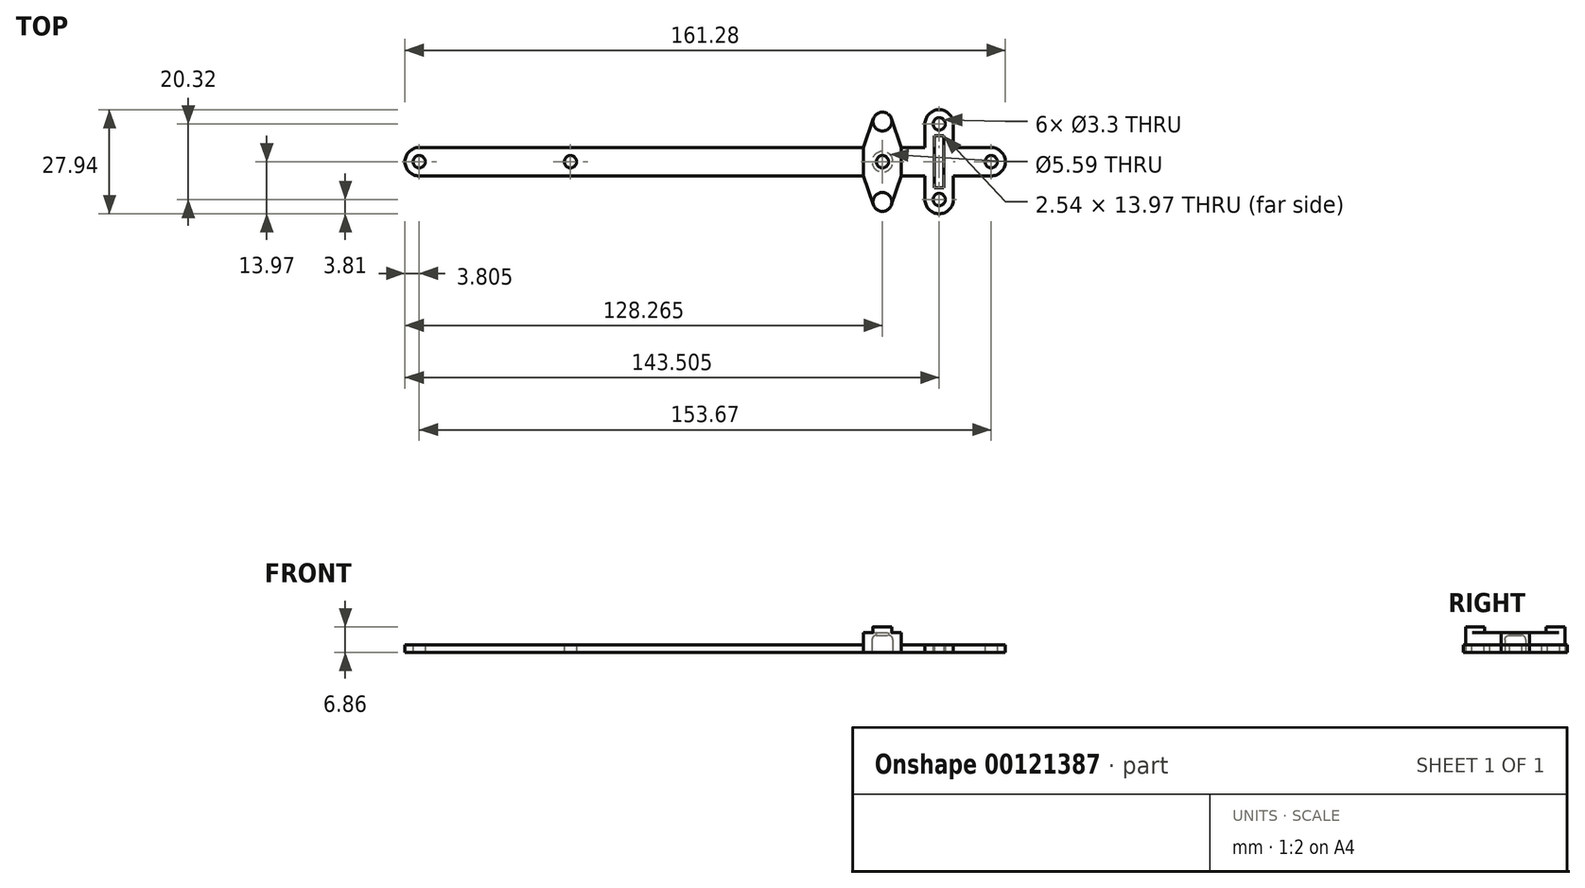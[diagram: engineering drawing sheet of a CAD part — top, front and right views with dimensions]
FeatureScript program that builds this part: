
annotation { "Feature Type Name" : "Feature", "Feature Type Description" : "" }
export const myFeature = defineFeature(function(context is Context, id is Id, definition is map)
    precondition{}
    {
        {
            var Q0;
            Q0=qCreatedBy(makeId("Top.planeOp"),FACE);
            var sketch = newSketch(context, id + "F0", { "sketchPlane" : qUnion([Q0])});
            skCircle(sketch, "E0", {"center": v(-76.83, 0) * mm, "radius": 1.65 * mm});
            skCircle(sketch, "E1", {"center": v(76.83, 0) * mm, "radius": 1.65 * mm});
            skLineSegment(sketch, "E2", {"start": v(-76.83, 0) * mm, "end": v(76.83, 0) * mm, "construction": true});
            skPoint(sketch, "E3", {"position": v(0, 0) * mm});
            skCircle(sketch, "E4", {"center": v(-36.2, 0) * mm, "radius": 1.65 * mm});
            skCircle(sketch, "E5", {"center": v(62.87, 10.16) * mm, "radius": 1.65 * mm});
            skCircle(sketch, "E6", {"center": v(62.87, -10.16) * mm, "radius": 1.65 * mm});
            skLineSegment(sketch, "E7", {"start": v(62.87, 10.16) * mm, "end": v(62.87, -10.16) * mm, "construction": true});
            skPoint(sketch, "E8", {"position": v(62.87, 0) * mm});
            skCircle(sketch, "E9", {"center": v(47.63, 0) * mm, "radius": 1.65 * mm});
            skLineSegment(sketch, "E10", {"start": v(-76.83, 3.8) * mm, "end": v(42.55, 3.8) * mm});
            skLineSegment(sketch, "E11", {"start": v(59.06, 3.81) * mm, "end": v(59.06, 10.16) * mm});
            skLineSegment(sketch, "E12", {"start": v(66.68, 10.16) * mm, "end": v(66.68, 3.8) * mm});
            skLineSegment(sketch, "E13", {"start": v(66.68, 3.8) * mm, "end": v(76.83, 3.81) * mm});
            skLineSegment(sketch, "E14", {"start": v(-76.83, -3.81) * mm, "end": v(42.55, -3.81) * mm});
            skLineSegment(sketch, "E15", {"start": v(59.06, -3.81) * mm, "end": v(59.06, -10.16) * mm});
            skLineSegment(sketch, "E16", {"start": v(66.68, -10.16) * mm, "end": v(66.68, -3.8) * mm});
            skLineSegment(sketch, "E17", {"start": v(66.68, -3.81) * mm, "end": v(76.84, -3.81) * mm});
            skArc(sketch, "E18", {"start": v(-76.83, 3.8) * mm, "mid": v(-80.64, 0) * mm, "end": v(-76.83, -3.8) * mm});
            skArc(sketch, "E19", {"start": v(66.68, 10.16) * mm, "mid": v(62.87, 13.97) * mm, "end": v(59.06, 10.16) * mm});
            skArc(sketch, "E20", {"start": v(59.06, -10.16) * mm, "mid": v(62.87, -13.97) * mm, "end": v(66.68, -10.16) * mm});
            skArc(sketch, "E21", {"start": v(76.83, -3.8) * mm, "mid": v(80.64, 0) * mm, "end": v(76.83, 3.8) * mm});
            skLineSegment(sketch, "E22", {"start": v(47.63, -10.8) * mm, "end": v(47.63, 10.8) * mm, "construction": true});
            skLineSegment(sketch, "E23", {"start": v(42.55, 3.8) * mm, "end": v(45.22, 11.62) * mm});
            skLineSegment(sketch, "E24", {"start": v(50.03, 11.62) * mm, "end": v(52.7, 3.8) * mm});
            skLineSegment(sketch, "E25", {"start": v(52.7, -3.81) * mm, "end": v(50.03, -11.62) * mm});
            skLineSegment(sketch, "E26", {"start": v(42.55, -3.81) * mm, "end": v(45.22, -11.62) * mm});
            skArc(sketch, "E27", {"start": v(45.22, 11.62) * mm, "mid": v(47.63, 8.25) * mm, "end": v(50.03, 11.62) * mm, "construction": true});
            skArc(sketch, "E28", {"start": v(50.03, 11.62) * mm, "mid": v(47.63, 13.33) * mm, "end": v(45.22, 11.62) * mm});
            skArc(sketch, "E29", {"start": v(45.22, -11.62) * mm, "mid": v(47.63, -13.34) * mm, "end": v(50.03, -11.62) * mm});
            skArc(sketch, "E30", {"start": v(50.03, -11.62) * mm, "mid": v(47.63, -8.26) * mm, "end": v(45.22, -11.62) * mm, "construction": true});
            skLineSegment(sketch, "E31", {"start": v(42.55, 3.8) * mm, "end": v(52.7, 3.8) * mm, "construction": true});
            skLineSegment(sketch, "E32", {"start": v(42.55, -3.81) * mm, "end": v(52.7, -3.81) * mm, "construction": true});
            skLineSegment(sketch, "E33", {"start": v(52.7, -3.81) * mm, "end": v(59.06, -3.81) * mm});
            skLineSegment(sketch, "E34", {"start": v(52.7, 3.8) * mm, "end": v(59.06, 3.8) * mm});
            skLineSegment(sketch, "E35.bottom", {"start": v(61.6, 6.99) * mm, "end": v(64.14, 6.99) * mm});
            skLineSegment(sketch, "E35.top", {"start": v(61.6, -6.99) * mm, "end": v(64.14, -6.99) * mm});
            skLineSegment(sketch, "E35.left", {"start": v(61.6, 6.99) * mm, "end": v(61.6, -6.99) * mm});
            skLineSegment(sketch, "E35.right", {"start": v(64.14, 6.99) * mm, "end": v(64.14, -6.99) * mm});
            skPoint(sketch, "E36", {"position": v(62.87, 6.99) * mm});
            skPoint(sketch, "E37", {"position": v(61.6, 0) * mm});
            skSolve(sketch);
        }
        {
            var Q0;
            Q0 = qSketchRegion(id + "F0", true);
            extrude(context, id + "F1", {"entities" : qUnion([Q0]), "depth" : 2.03 * mm});
        }
        {
            var Q0;
            Q0=makeQuery(id+"F1.opExtrude","CAP_FACE",FACE,{"disambiguationData":[OSD([sQuery(id+"F0.wireOp",EDGE,"E0"),sQuery(id+"F0.wireOp",EDGE,"E1"),sQuery(id+"F0.wireOp",EDGE,"E4"),sQuery(id+"F0.wireOp",EDGE,"E5"),sQuery(id+"F0.wireOp",EDGE,"E6"),sQuery(id+"F0.wireOp",EDGE,"E9"),sQuery(id+"F0.wireOp",EDGE,"E10"),sQuery(id+"F0.wireOp",EDGE,"E11"),sQuery(id+"F0.wireOp",EDGE,"E12"),sQuery(id+"F0.wireOp",EDGE,"E13"),sQuery(id+"F0.wireOp",EDGE,"E14"),sQuery(id+"F0.wireOp",EDGE,"E15"),sQuery(id+"F0.wireOp",EDGE,"E16"),sQuery(id+"F0.wireOp",EDGE,"E17"),sQuery(id+"F0.wireOp",EDGE,"E18"),sQuery(id+"F0.wireOp",EDGE,"E19"),sQuery(id+"F0.wireOp",EDGE,"E20"),sQuery(id+"F0.wireOp",EDGE,"E21"),sQuery(id+"F0.wireOp",EDGE,"E23"),sQuery(id+"F0.wireOp",EDGE,"E24"),sQuery(id+"F0.wireOp",EDGE,"E25"),sQuery(id+"F0.wireOp",EDGE,"E26"),sQuery(id+"F0.wireOp",EDGE,"E28"),sQuery(id+"F0.wireOp",EDGE,"E29"),sQuery(id+"F0.wireOp",EDGE,"E33"),sQuery(id+"F0.wireOp",EDGE,"E34")])],"isStart":false});
            var sketch = newSketch(context, id + "F2", { "sketchPlane" : qUnion([Q0])});
            skLineSegment(sketch, "E38", {"start": v(45.22, 11.62) * mm, "end": v(42.55, 3.8) * mm});
            skLineSegment(sketch, "E39", {"start": v(42.55, 3.8) * mm, "end": v(42.55, -3.81) * mm});
            skLineSegment(sketch, "E40", {"start": v(42.55, -3.81) * mm, "end": v(45.22, -11.62) * mm});
            skLineSegment(sketch, "E41", {"start": v(50.03, 11.62) * mm, "end": v(52.7, 3.8) * mm});
            skLineSegment(sketch, "E42", {"start": v(52.7, 3.8) * mm, "end": v(52.7, -3.81) * mm});
            skLineSegment(sketch, "E43", {"start": v(52.7, -3.81) * mm, "end": v(50.03, -11.62) * mm});
            skArc(sketch, "E44", {"start": v(50.03, 11.62) * mm, "mid": v(47.63, 13.34) * mm, "end": v(45.22, 11.62) * mm});
            skArc(sketch, "E45", {"start": v(45.22, -11.62) * mm, "mid": v(47.63, -13.34) * mm, "end": v(50.03, -11.62) * mm});
            skCircle(sketch, "E46", {"center": v(47.63, 0) * mm, "radius": 1.65 * mm});
            skSolve(sketch);
        }
        {
            var Q0;
            Q0 = qSketchRegion(id + "F2", true);
            extrude(context, id + "F3", {"entities" : qUnion([Q0]), "operationType" : NewBodyOperationType.ADD, "depth" : 3.3 * mm});
        }
        {
            var Q0;
            Q0=makeQuery(id+"F3.opExtrude","CAP_FACE",FACE,{"disambiguationData":[OSD([sQuery(id+"F2.wireOp",EDGE,"E38"),sQuery(id+"F2.wireOp",EDGE,"E39"),sQuery(id+"F2.wireOp",EDGE,"E40"),sQuery(id+"F2.wireOp",EDGE,"E41"),sQuery(id+"F2.wireOp",EDGE,"E42"),sQuery(id+"F2.wireOp",EDGE,"E43"),sQuery(id+"F2.wireOp",EDGE,"E44"),sQuery(id+"F2.wireOp",EDGE,"E45"),sQuery(id+"F2.wireOp",EDGE,"E46")])],"isStart":false});
            var sketch = newSketch(context, id + "F4", { "sketchPlane" : qUnion([Q0])});
            skCircle(sketch, "E47", {"center": v(47.63, 10.8) * mm, "radius": 2.54 * mm});
            skCircle(sketch, "E48", {"center": v(47.63, -10.8) * mm, "radius": 2.54 * mm});
            skSolve(sketch);
        }
        {
            var Q0;
            Q0 = qSketchRegion(id + "F4", true);
            extrude(context, id + "F5", {"entities" : qUnion([Q0]), "operationType" : NewBodyOperationType.ADD, "depth" : 1.52 * mm});
        }
        {
            var Q0;
            Q0=makeQuery(id+"F1.opExtrude","CAP_FACE",FACE,{"disambiguationData":[OSD([sQuery(id+"F0.wireOp",EDGE,"E0"),sQuery(id+"F0.wireOp",EDGE,"E1"),sQuery(id+"F0.wireOp",EDGE,"E4"),sQuery(id+"F0.wireOp",EDGE,"E5"),sQuery(id+"F0.wireOp",EDGE,"E6"),sQuery(id+"F0.wireOp",EDGE,"E9"),sQuery(id+"F0.wireOp",EDGE,"E10"),sQuery(id+"F0.wireOp",EDGE,"E11"),sQuery(id+"F0.wireOp",EDGE,"E12"),sQuery(id+"F0.wireOp",EDGE,"E13"),sQuery(id+"F0.wireOp",EDGE,"E14"),sQuery(id+"F0.wireOp",EDGE,"E15"),sQuery(id+"F0.wireOp",EDGE,"E16"),sQuery(id+"F0.wireOp",EDGE,"E17"),sQuery(id+"F0.wireOp",EDGE,"E18"),sQuery(id+"F0.wireOp",EDGE,"E19"),sQuery(id+"F0.wireOp",EDGE,"E20"),sQuery(id+"F0.wireOp",EDGE,"E21"),sQuery(id+"F0.wireOp",EDGE,"E23"),sQuery(id+"F0.wireOp",EDGE,"E24"),sQuery(id+"F0.wireOp",EDGE,"E25"),sQuery(id+"F0.wireOp",EDGE,"E26"),sQuery(id+"F0.wireOp",EDGE,"E28"),sQuery(id+"F0.wireOp",EDGE,"E29"),sQuery(id+"F0.wireOp",EDGE,"E33"),sQuery(id+"F0.wireOp",EDGE,"E34")])],"isStart":true});
            var sketch = newSketch(context, id + "F6", { "sketchPlane" : qUnion([Q0])});
            skCircle(sketch, "E49", {"center": v(47.63, 0) * mm, "radius": 2.8 * mm});
            skSolve(sketch);
        }
        {
            var Q0;
            Q0 = qSketchRegion(id + "F6", true);
            extrude(context, id + "F7", {"entities" : qUnion([Q0]), "operationType" : NewBodyOperationType.REMOVE, "oppositeDirection" : true, "depth" : 4.57 * mm});
        }
        {
            var Q0;
            Q0=makeQuery(id+"F7.boolean.opBoolean","COPY",EDGE,{"derivedFrom":makeQuery(id+"F7.opExtrude","CAP_EDGE",EDGE,{"disambiguationData":[OSD([sQuery(id+"F6.wireOp",EDGE,"E49")])],"isStart":false})});
            fillet(context, id + "F8", {"entities" : qUnion([Q0]), "radius" : 1.14 * mm, "tangentPropagation" : true, "allowEdgeOverflow" : false});
        }
    });
